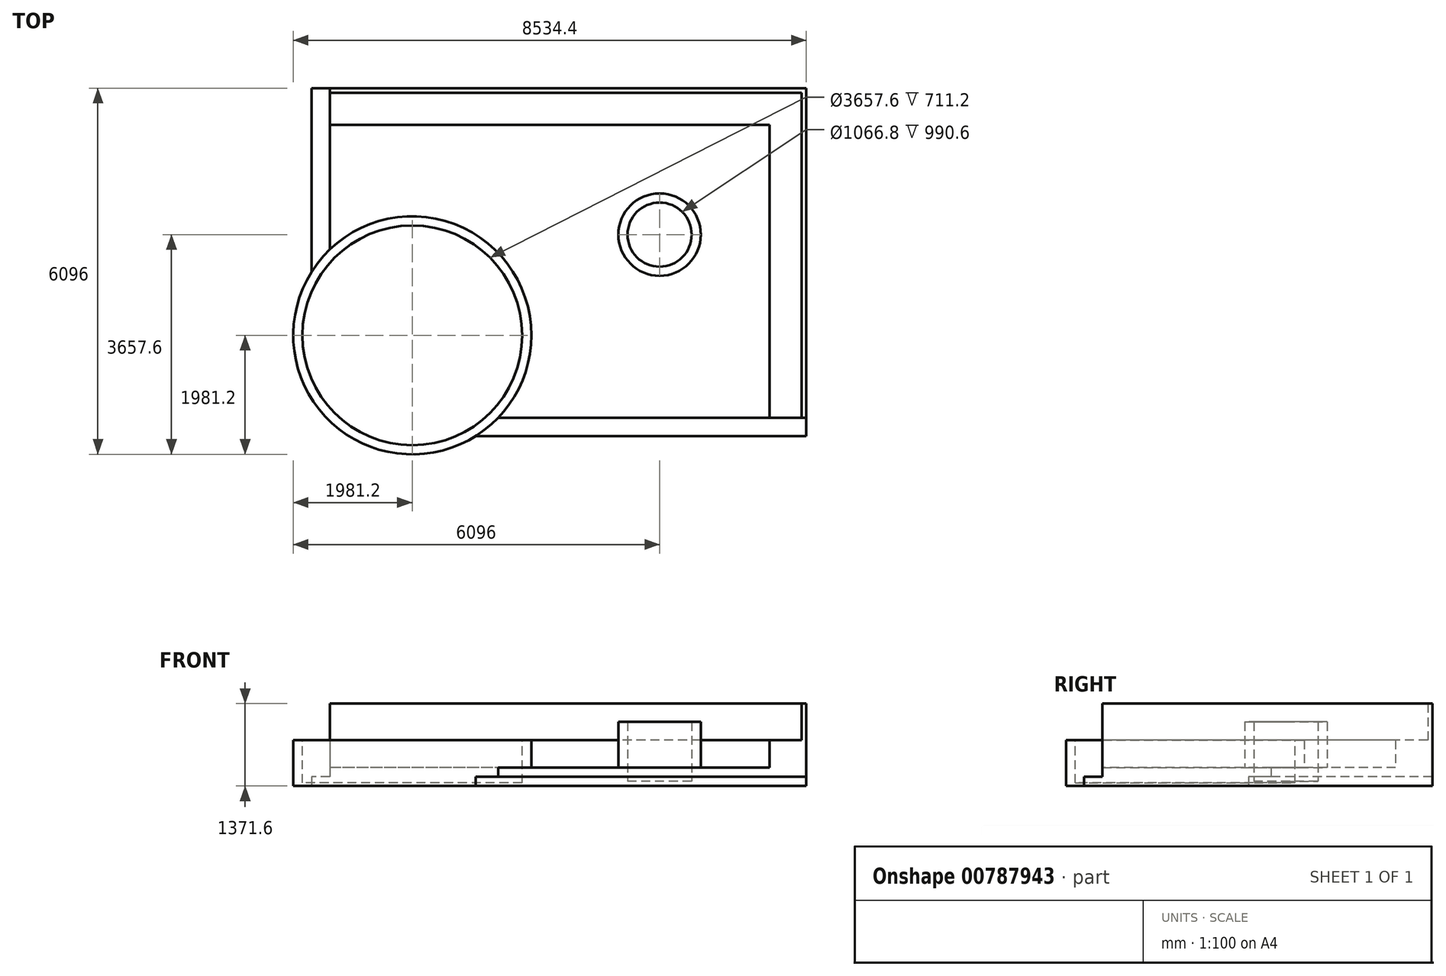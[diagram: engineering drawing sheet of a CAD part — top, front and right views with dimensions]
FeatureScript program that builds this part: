
annotation { "Feature Type Name" : "Feature", "Feature Type Description" : "" }
export const myFeature = defineFeature(function(context is Context, id is Id, definition is map)
    precondition{}
    {
        {
            var Q0;
            Q0=qCreatedBy(makeId("Top.planeOp"),FACE);
            var sketch = newSketch(context, id + "F0", { "sketchPlane" : qUnion([Q0])});
            skLineSegment(sketch, "E0.bottom", {"start": v(-3048, 2438.4) * mm, "end": v(4876.8, 2438.4) * mm});
            skLineSegment(sketch, "E0.left", {"start": v(-3048, 2438.4) * mm, "end": v(-3048, -304.8) * mm});
            skLineSegment(sketch, "E0.right", {"start": v(4876.8, 2438.4) * mm, "end": v(4876.8, -3048) * mm});
            skLineSegment(sketch, "E1", {"start": v(-3048, -304.8) * mm, "end": v(-304.8, -3048) * mm});
            skLineSegment(sketch, "E2", {"start": v(-304.8, -3048) * mm, "end": v(4876.8, -3048) * mm});
            skSolve(sketch);
        }
        {
            var Q0;
            Q0 = qSketchRegion(id + "F0", true);
            extrude(context, id + "F1", {"entities" : qUnion([Q0]), "depth" : 304.8 * mm, "offsetDistance" : 25.4 * mm});
        }
        {
            var Q0;
            Q0=makeQuery(id+"F1.opExtrude","CAP_FACE",FACE,{"disambiguationData":[OSD([sQuery(id+"F0.wireOp",EDGE,"E0.bottom"),sQuery(id+"F0.wireOp",EDGE,"E0.left"),sQuery(id+"F0.wireOp",EDGE,"E0.right"),sQuery(id+"F0.wireOp",EDGE,"E1"),sQuery(id+"F0.wireOp",EDGE,"E2")])],"isStart":false});
            var sketch = newSketch(context, id + "F2", { "sketchPlane" : qUnion([Q0])});
            skLineSegment(sketch, "E3.bottom", {"start": v(4876.8, 2438.4) * mm, "end": v(-3048, 2438.4) * mm});
            skLineSegment(sketch, "E3.top", {"start": v(4876.8, 1828.8) * mm, "end": v(-3048, 1828.8) * mm});
            skLineSegment(sketch, "E3.left", {"start": v(4876.8, 2438.4) * mm, "end": v(4876.8, 1828.8) * mm});
            skLineSegment(sketch, "E3.right", {"start": v(-3048, 2438.4) * mm, "end": v(-3048, 1828.8) * mm});
            skLineSegment(sketch, "E4.bottom", {"start": v(4876.8, 2438.4) * mm, "end": v(4267.2, 2438.4) * mm});
            skLineSegment(sketch, "E4.top", {"start": v(4876.8, -3048) * mm, "end": v(4267.2, -3048) * mm});
            skLineSegment(sketch, "E4.left", {"start": v(4876.8, 2438.4) * mm, "end": v(4876.8, -3048) * mm});
            skLineSegment(sketch, "E4.right", {"start": v(4267.2, 2438.4) * mm, "end": v(4267.2, -3048) * mm});
            skSolve(sketch);
        }
        {
            var Q0;
            Q0 = qSketchRegion(id + "F2", true);
            extrude(context, id + "F3", {"entities" : qUnion([Q0]), "operationType" : NewBodyOperationType.ADD, "depth" : 457.2 * mm, "offsetDistance" : 30.48 * mm});
        }
        {
            var Q0;
            Q0=makeQuery(id+"F3.opExtrude","CAP_FACE",FACE,{"disambiguationData":[OSD([sQuery(id+"F2.wireOp",EDGE,"E3.bottom"),sQuery(id+"F2.wireOp",EDGE,"E3.top"),sQuery(id+"F2.wireOp",EDGE,"E3.right"),sQuery(id+"F2.wireOp",EDGE,"E4.bottom"),sQuery(id+"F2.wireOp",EDGE,"E4.top"),sQuery(id+"F2.wireOp",EDGE,"E4.left"),sQuery(id+"F2.wireOp",EDGE,"E4.right")])],"isStart":false});
            var sketch = newSketch(context, id + "F4", { "sketchPlane" : qUnion([Q0])});
            skLineSegment(sketch, "E5.bottom", {"start": v(-3048, 2438.4) * mm, "end": v(4876.8, 2438.4) * mm});
            skLineSegment(sketch, "E5.top", {"start": v(-3048, 2362.2) * mm, "end": v(4876.8, 2362.2) * mm});
            skLineSegment(sketch, "E5.left", {"start": v(-3048, 2438.4) * mm, "end": v(-3048, 2362.2) * mm});
            skLineSegment(sketch, "E5.right", {"start": v(4876.8, 2438.4) * mm, "end": v(4876.8, 2362.2) * mm});
            skLineSegment(sketch, "E6.bottom", {"start": v(4876.8, 2438.4) * mm, "end": v(4800.6, 2438.4) * mm});
            skLineSegment(sketch, "E6.top", {"start": v(4876.8, -3048) * mm, "end": v(4800.6, -3048) * mm});
            skLineSegment(sketch, "E6.left", {"start": v(4876.8, 2438.4) * mm, "end": v(4876.8, -3048) * mm});
            skLineSegment(sketch, "E6.right", {"start": v(4800.6, 2438.4) * mm, "end": v(4800.6, -3048) * mm});
            skSolve(sketch);
        }
        {
            var Q0;
            Q0 = qSketchRegion(id + "F4", true);
            extrude(context, id + "F5", {"entities" : qUnion([Q0]), "operationType" : NewBodyOperationType.ADD, "depth" : 609.6 * mm, "offsetDistance" : 30.48 * mm});
        }
        {
            var Q0;
            Q0=qCreatedBy(makeId("Top.planeOp"),FACE);
            var sketch = newSketch(context, id + "F6", { "sketchPlane" : qUnion([Q0])});
            skLineSegment(sketch, "E7.bottom", {"start": v(-3048, 2438.4) * mm, "end": v(-3352.8, 2438.4) * mm});
            skLineSegment(sketch, "E7.top", {"start": v(-3048, -1100.66) * mm, "end": v(-3352.8, -1100.66) * mm});
            skLineSegment(sketch, "E7.left", {"start": v(-3048, 2438.4) * mm, "end": v(-3048, -1100.66) * mm});
            skLineSegment(sketch, "E7.right", {"start": v(-3352.8, 2438.4) * mm, "end": v(-3352.8, -1100.66) * mm});
            skLineSegment(sketch, "E8.bottom", {"start": v(4876.8, -3048) * mm, "end": v(-1355, -3048) * mm});
            skLineSegment(sketch, "E8.top", {"start": v(4876.8, -3352.8) * mm, "end": v(-1355, -3352.8) * mm});
            skLineSegment(sketch, "E8.left", {"start": v(4876.8, -3048) * mm, "end": v(4876.8, -3352.8) * mm});
            skLineSegment(sketch, "E8.right", {"start": v(-1355, -3048) * mm, "end": v(-1355, -3352.8) * mm});
            skSolve(sketch);
        }
        {
            var Q0;
            Q0=makeQuery(id+"F6.imprint","IMPRINT",FACE,{"disambiguationData":[TD([[makeQuery(id+"F6.imprint","IMPRINT",EDGE,{"derivedFrom":sQuery(id+"F6.wireOp",EDGE,"E7.bottom")}),1.0]])]});
            var Q1;
            Q1=makeQuery(id+"F6.imprint","IMPRINT",FACE,{"disambiguationData":[TD([[makeQuery(id+"F6.imprint","IMPRINT",EDGE,{"derivedFrom":sQuery(id+"F6.wireOp",EDGE,"E8.bottom")}),1.0]])]});
            extrude(context, id + "F7", {"entities" : qUnion([Q0, Q1]), "operationType" : NewBodyOperationType.ADD, "depth" : 152.4 * mm, "offsetDistance" : 30.48 * mm});
        }
        {
            var Q0;
            Q0=qCreatedBy(makeId("Top.planeOp"),FACE);
            var sketch = newSketch(context, id + "F8", { "sketchPlane" : qUnion([Q0])});
            skCircle(sketch, "E9", {"center": v(-1676.4, -1676.4) * mm, "radius": 1981.2 * mm});
            skSolve(sketch);
        }
        {
            var Q0;
            Q0 = qSketchRegion(id + "F8", true);
            extrude(context, id + "F9", {"entities" : qUnion([Q0]), "operationType" : NewBodyOperationType.REMOVE, "endBound" : BoundingType.THROUGH_ALL, "depth" : 30.48 * mm, "offsetDistance" : 30.48 * mm});
        }
        {
            var Q0;
            Q0=qCreatedBy(makeId("Top.planeOp"),FACE);
            var sketch = newSketch(context, id + "F10", { "sketchPlane" : qUnion([Q0])});
            skCircle(sketch, "E10", {"center": v(-1676.4, -1676.4) * mm, "radius": 1981.2 * mm});
            skSolve(sketch);
        }
        {
            var Q0;
            Q0 = qSketchRegion(id + "F10", true);
            extrude(context, id + "F11", {"entities" : qUnion([Q0]), "operationType" : NewBodyOperationType.ADD, "depth" : 762 * mm, "offsetDistance" : 30.48 * mm});
        }
        {
            var Q0;
            Q0=makeQuery(id+"F11.opExtrude","CAP_FACE",FACE,{"disambiguationData":[OSD([sQuery(id+"F10.wireOp",EDGE,"E10")])],"isStart":false});
            var sketch = newSketch(context, id + "F12", { "sketchPlane" : qUnion([Q0])});
            skCircle(sketch, "E11", {"center": v(-1676.4, -1676.4) * mm, "radius": 1828.8 * mm});
            skSolve(sketch);
        }
        {
            var Q0;
            Q0 = qSketchRegion(id + "F12", true);
            extrude(context, id + "F13", {"entities" : qUnion([Q0]), "operationType" : NewBodyOperationType.REMOVE, "oppositeDirection" : true, "depth" : 711.2 * mm, "offsetDistance" : 30.48 * mm});
        }
        {
            var Q0;
            Q0=makeQuery(id+"F1.opExtrude","CAP_FACE",FACE,{"disambiguationData":[OSD([sQuery(id+"F0.wireOp",EDGE,"E0.bottom"),sQuery(id+"F0.wireOp",EDGE,"E0.left"),sQuery(id+"F0.wireOp",EDGE,"E0.right"),sQuery(id+"F0.wireOp",EDGE,"E1"),sQuery(id+"F0.wireOp",EDGE,"E2")])],"isStart":false});
            var sketch = newSketch(context, id + "F14", { "sketchPlane" : qUnion([Q0])});
            skCircle(sketch, "E12", {"center": v(2438.4, 0) * mm, "radius": 685.8 * mm});
            skCircle(sketch, "E13", {"center": v(2438.4, 0) * mm, "radius": 533.4 * mm});
            skSolve(sketch);
        }
        {
            var Q0;
            Q0 = qSketchRegion(id + "F14", true);
            extrude(context, id + "F15", {"entities" : qUnion([Q0]), "operationType" : NewBodyOperationType.ADD, "depth" : 762 * mm, "offsetDistance" : 30.48 * mm});
        }
        {
            var Q0;
            Q0=makeQuery(id+"F15.boolean.opBoolean","SPLIT",FACE,{"disambiguationData":[TD([makeQuery(id+"F15.opExtrude","SWEPT_FACE",FACE,{"disambiguationData":[OSD([sQuery(id+"F14.wireOp",EDGE,"E13")])]})])],"derivedFrom":makeQuery(id+"F1.opExtrude","CAP_FACE",FACE,{"disambiguationData":[OSD([sQuery(id+"F0.wireOp",EDGE,"E0.bottom"),sQuery(id+"F0.wireOp",EDGE,"E0.left"),sQuery(id+"F0.wireOp",EDGE,"E0.right"),sQuery(id+"F0.wireOp",EDGE,"E1"),sQuery(id+"F0.wireOp",EDGE,"E2")])],"isStart":false})});
            var sketch = newSketch(context, id + "F16", { "sketchPlane" : qUnion([Q0])});
            skCircle(sketch, "E14", {"center": v(2438.4, 0) * mm, "radius": 533.4 * mm});
            skSolve(sketch);
        }
        {
            var Q0;
            Q0 = qSketchRegion(id + "F16", true);
            extrude(context, id + "F17", {"entities" : qUnion([Q0]), "operationType" : NewBodyOperationType.REMOVE, "oppositeDirection" : true, "depth" : 228.6 * mm, "offsetDistance" : 30.48 * mm});
        }
    });
